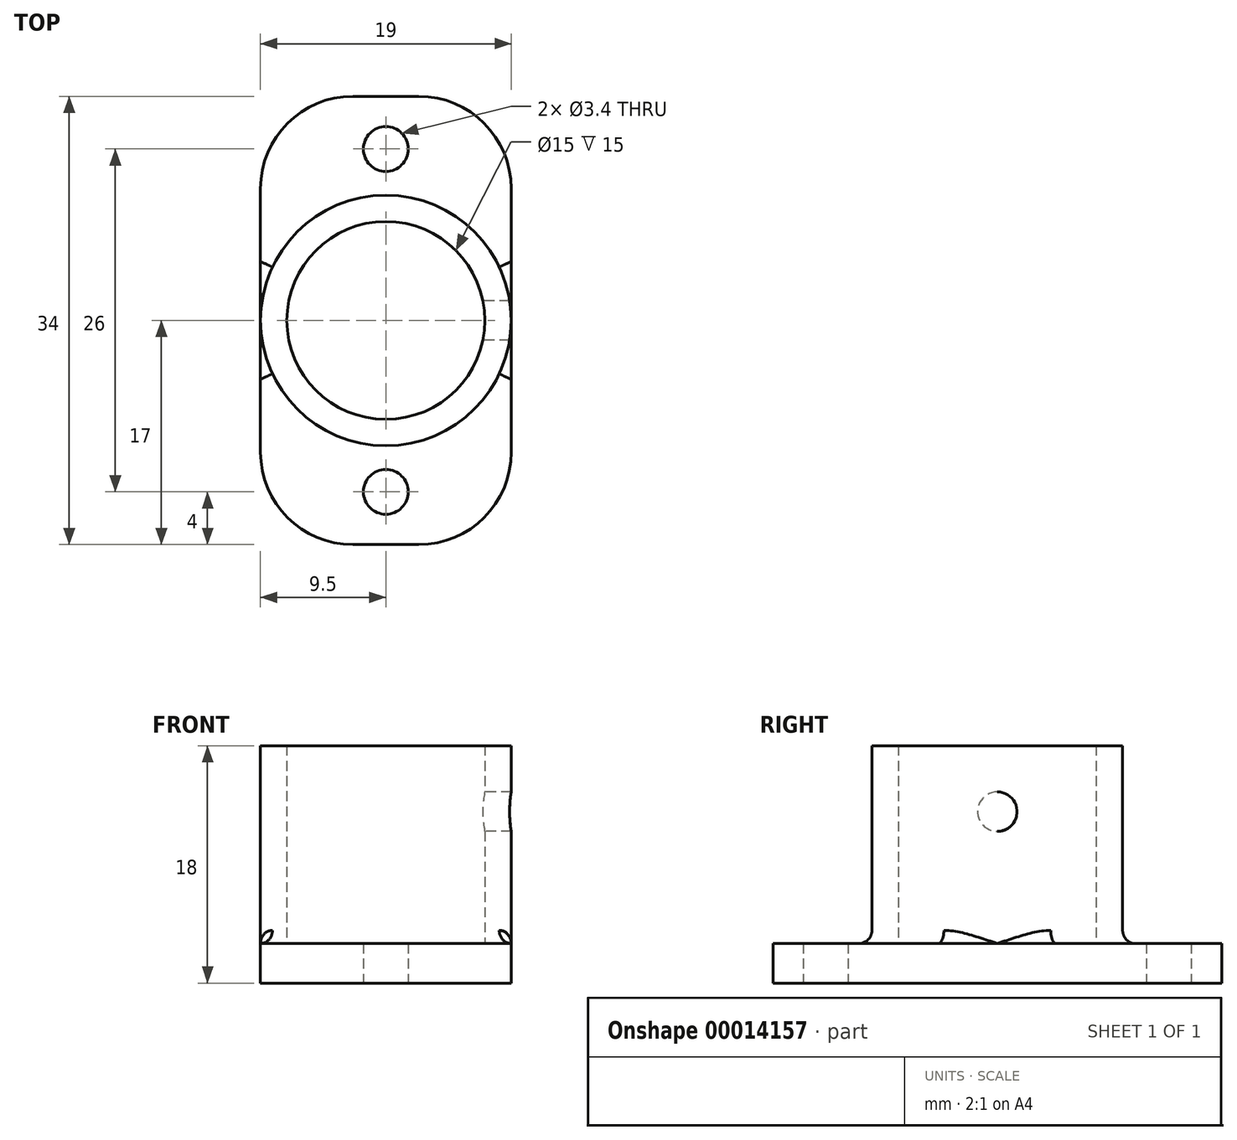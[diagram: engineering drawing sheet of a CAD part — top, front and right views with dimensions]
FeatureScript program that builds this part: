
annotation { "Feature Type Name" : "Feature", "Feature Type Description" : "" }
export const myFeature = defineFeature(function(context is Context, id is Id, definition is map)
    precondition{}
    {
        {
            var Q0;
            Q0=qCreatedBy(makeId("Top.planeOp"),FACE);
            var sketch = newSketch(context, id + "F0", { "sketchPlane" : qUnion([Q0])});
            skLineSegment(sketch, "E0.rect.bottom", {"start": v(9.5, 17) * mm, "end": v(-9.5, 17) * mm});
            skLineSegment(sketch, "E0.rect.top", {"start": v(9.5, -17) * mm, "end": v(-9.5, -17) * mm});
            skLineSegment(sketch, "E0.rect.left", {"start": v(9.5, 17) * mm, "end": v(9.5, -17) * mm});
            skLineSegment(sketch, "E0.rect.right", {"start": v(-9.5, 17) * mm, "end": v(-9.5, -17) * mm});
            skPoint(sketch, "E0.rect.middle", {"position": v(0, 0) * mm});
            skLineSegment(sketch, "E1", {"start": v(0, 17) * mm, "end": v(0, -17) * mm, "construction": true});
            skLineSegment(sketch, "E2", {"start": v(-9.5, 0) * mm, "end": v(9.5, 0) * mm, "construction": true});
            skCircle(sketch, "E3", {"center": v(0, 13) * mm, "radius": 1.7 * mm});
            skCircle(sketch, "E4.0.MirrorC", {"center": v(0, -13) * mm, "radius": 1.7 * mm});
            skSolve(sketch);
        }
        {
            var Q0;
            Q0=makeQuery(id+"F0.imprint","IMPRINT",FACE,{"disambiguationData":[TD([[makeQuery(id+"F0.imprint","IMPRINT",EDGE,{"derivedFrom":sQuery(id+"F0.wireOp",EDGE,"E0.rect.bottom")}),1.0]])]});
            extrude(context, id + "F1", {"entities" : qUnion([Q0]), "depth" : 3 * mm});
        }
        {
            var Q0;
            Q0=makeQuery(id+"F1.opExtrude","CAP_FACE",FACE,{"disambiguationData":[OSD([sQuery(id+"F0.wireOp",EDGE,"E0.rect.bottom"),sQuery(id+"F0.wireOp",EDGE,"E0.rect.top"),sQuery(id+"F0.wireOp",EDGE,"E0.rect.left"),sQuery(id+"F0.wireOp",EDGE,"E0.rect.right")])],"isStart":false});
            var sketch = newSketch(context, id + "F2", { "sketchPlane" : qUnion([Q0])});
            skCircle(sketch, "E5", {"center": v(0, 0) * mm, "radius": 9.5 * mm});
            skCircle(sketch, "E6", {"center": v(0, 0) * mm, "radius": 7.5 * mm});
            skSolve(sketch);
        }
        {
            var Q0;
            Q0=qSketchRegion(id+"F2",true);
            extrude(context, id + "F3", {"entities" : qUnion([Q0]), "operationType" : NewBodyOperationType.ADD, "depth" : 15 * mm});
        }
        {
            var Q0;
            Q0=qCreatedBy(makeId("Right.planeOp"),FACE);
            var sketch = newSketch(context, id + "F4", { "sketchPlane" : qUnion([Q0])});
            skCircle(sketch, "E7", {"center": v(0, 13) * mm, "radius": 1.5 * mm});
            skSolve(sketch);
        }
        {
            var Q0;
            Q0=makeQuery(id+"F4.imprint","IMPRINT",FACE,{"disambiguationData":[TD([[makeQuery(id+"F4.imprint","IMPRINT",EDGE,{"derivedFrom":sQuery(id+"F4.wireOp",EDGE,"E7")}),1.0]])]});
            extrude(context, id + "F5", {"entities" : qUnion([Q0]), "operationType" : NewBodyOperationType.REMOVE, "endBound" : BoundingType.THROUGH_ALL, "depth" : 25 * mm});
        }
        {
            var Q0;
            Q0=makeQuery(id+"F1.opExtrude","SWEPT_EDGE",EDGE,{"disambiguationData":[OSD([sQuery(id+"F0.wireOp",EDGE,"E0.rect.top"),sQuery(id+"F0.wireOp",EDGE,"E0.rect.left")])]});
            var Q1;
            Q1=makeQuery(id+"F1.opExtrude","SWEPT_EDGE",EDGE,{"disambiguationData":[OSD([sQuery(id+"F0.wireOp",EDGE,"E0.rect.bottom"),sQuery(id+"F0.wireOp",EDGE,"E0.rect.left")])]});
            var Q2;
            Q2=makeQuery(id+"F1.opExtrude","SWEPT_EDGE",EDGE,{"disambiguationData":[OSD([sQuery(id+"F0.wireOp",EDGE,"E0.rect.top"),sQuery(id+"F0.wireOp",EDGE,"E0.rect.right")])]});
            var Q3;
            Q3=makeQuery(id+"F1.opExtrude","SWEPT_EDGE",EDGE,{"disambiguationData":[OSD([sQuery(id+"F0.wireOp",EDGE,"E0.rect.bottom"),sQuery(id+"F0.wireOp",EDGE,"E0.rect.right")])]});
            fillet(context, id + "F6", {"entities" : qUnion([Q0, Q1, Q2, Q3]), "radius" : 7 * mm, "tangentPropagation" : true, "allowEdgeOverflow" : false});
        }
        {
            var Q0;
            Q0=makeQuery(id+"F3.boolean.opBoolean","SPLIT",EDGE,{"disambiguationData":[OD(1.0)],"derivedFrom":makeQuery(id+"F3.opExtrude","CAP_EDGE",EDGE,{"disambiguationData":[OSD([sQuery(id+"F2.wireOp",EDGE,"E5")])],"isStart":true})});
            fillet(context, id + "F7", {"entities" : qUnion([Q0]), "radius" : 1 * mm, "tangentPropagation" : true, "allowEdgeOverflow" : false});
        }
    });
